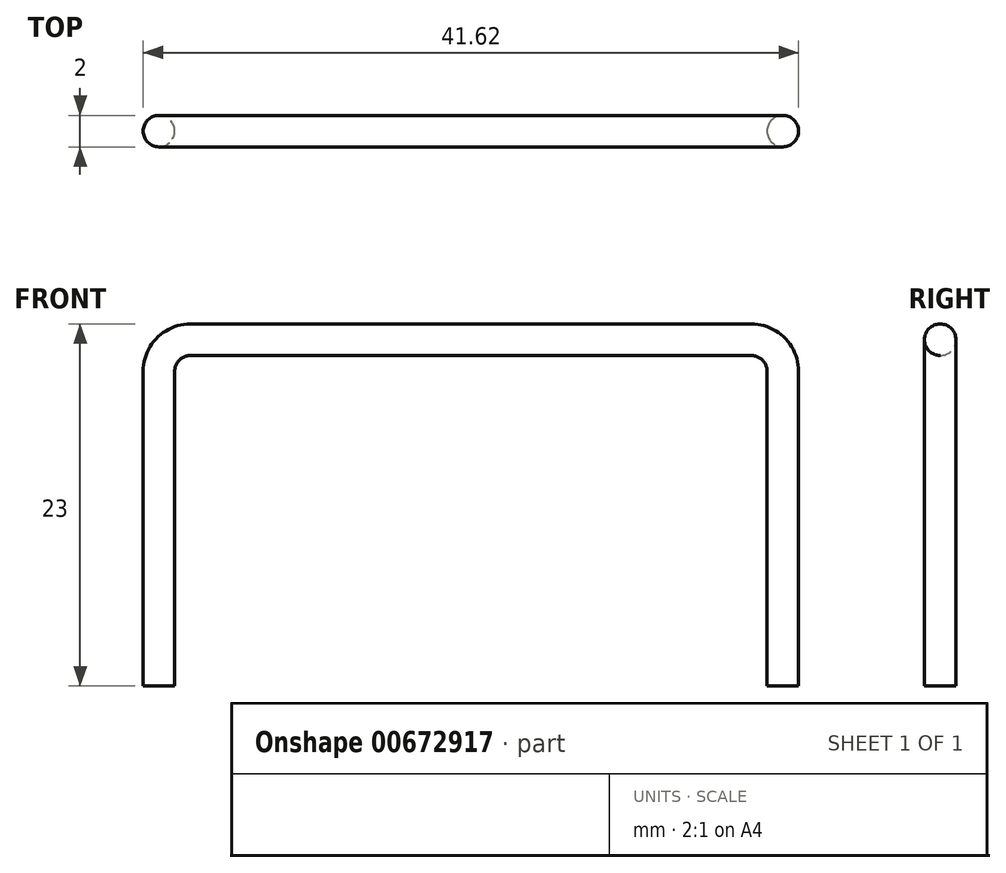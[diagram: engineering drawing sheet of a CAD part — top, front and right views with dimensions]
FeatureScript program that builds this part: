
annotation { "Feature Type Name" : "Feature", "Feature Type Description" : "" }
export const myFeature = defineFeature(function(context is Context, id is Id, definition is map)
    precondition{}
    {
        {
            var Q0;
            Q0=qCreatedBy(makeId("Top.planeOp"),FACE);
            var sketch = newSketch(context, id + "F0", { "sketchPlane" : qUnion([Q0])});
            skCircle(sketch, "E0", {"center": v(-19.81, 0) * mm, "radius": 1 * mm});
            skCircle(sketch, "E1.MirrorC", {"center": v(19.81, 0) * mm, "radius": 1 * mm});
            skSolve(sketch);
        }
        {
            var Q0;
            Q0=qCreatedBy(makeId("Front.planeOp"),FACE);
            var sketch = newSketch(context, id + "F1", { "sketchPlane" : qUnion([Q0])});
            skLineSegment(sketch, "E2", {"start": v(-19.81, 0) * mm, "end": v(-19.81, 20) * mm});
            skLineSegment(sketch, "E3", {"start": v(-17.81, 22) * mm, "end": v(0, 22) * mm});
            skPoint(sketch, "E4.visualSharp", {"position": v(-19.81, 22) * mm});
            skArc(sketch, "E4.filletArc", {"start": v(-17.81, 22) * mm, "mid": v(-19.23, 21.41) * mm, "end": v(-19.81, 20) * mm});
            skLineSegment(sketch, "E5.MirrorCS", {"start": v(17.81, 22) * mm, "end": v(0, 22) * mm});
            skArc(sketch, "E6.MirrorCS", {"start": v(17.81, 22) * mm, "mid": v(19.23, 21.41) * mm, "end": v(19.81, 20) * mm});
            skLineSegment(sketch, "E7.MirrorCS", {"start": v(19.81, 0) * mm, "end": v(19.81, 20) * mm});
            skSolve(sketch);
        }
        {
            var Q0;
            Q0=makeQuery(id+"F0.imprint","IMPRINT",FACE,{"disambiguationData":[TD([[makeQuery(id+"F0.imprint","IMPRINT",EDGE,{"derivedFrom":sQuery(id+"F0.wireOp",EDGE,"E0")}),1.0]])]});
            var Q1;
            Q1=sQuery(id+"F1.wireOp",EDGE,"E2");
            var Q2;
            Q2=sQuery(id+"F1.wireOp",EDGE,"E4.filletArc");
            var Q3;
            Q3=sQuery(id+"F1.wireOp",EDGE,"E3");
            var Q4;
            Q4=sQuery(id+"F1.wireOp",EDGE,"E5.MirrorCS");
            var Q5;
            Q5=sQuery(id+"F1.wireOp",EDGE,"E6.MirrorCS");
            var Q6;
            Q6=sQuery(id+"F1.wireOp",EDGE,"E7.MirrorCS");
            sweep(context, id + "F2", {"profiles" : qUnion([Q0]), "path" : qUnion([Q1, Q2, Q3, Q4, Q5, Q6])});
        }
    });
